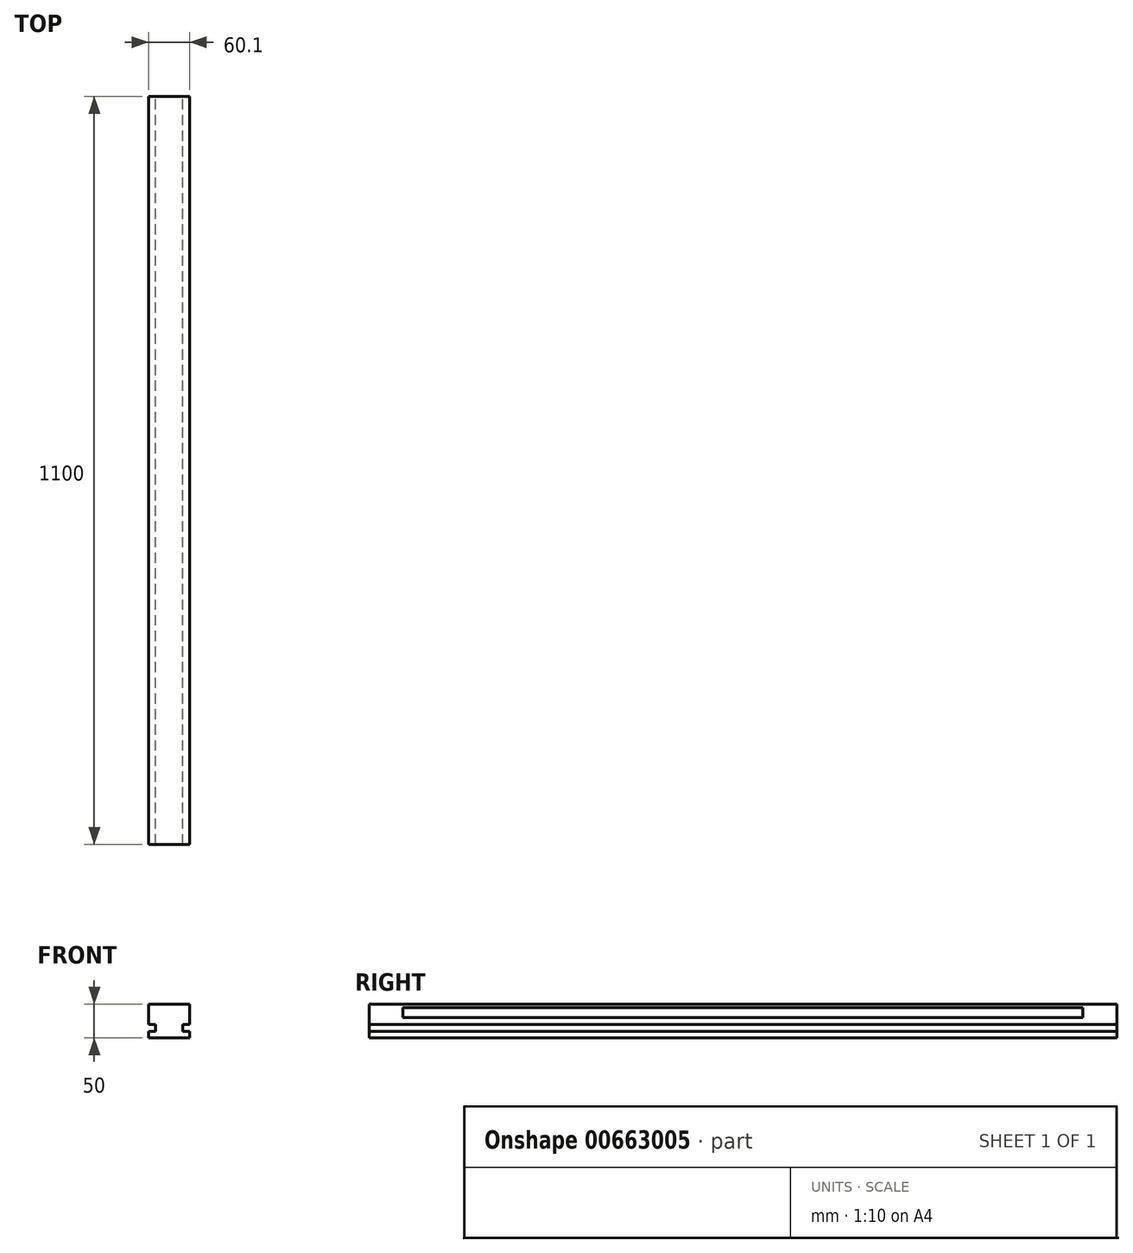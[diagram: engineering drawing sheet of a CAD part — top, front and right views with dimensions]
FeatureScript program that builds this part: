
annotation { "Feature Type Name" : "Feature", "Feature Type Description" : "" }
export const myFeature = defineFeature(function(context is Context, id is Id, definition is map)
    precondition{}
    {
        {
            var Q0;
            Q0=qCreatedBy(makeId("Front.planeOp"),FACE);
            var sketch = newSketch(context, id + "F0", { "sketchPlane" : qUnion([Q0])});
            skLineSegment(sketch, "E0", {"start": v(0, 0) * mm, "end": v(30, 0) * mm});
            skLineSegment(sketch, "E1", {"start": v(30, 0) * mm, "end": v(30, -30) * mm});
            skLineSegment(sketch, "E2", {"start": v(30, -30) * mm, "end": v(20, -30) * mm});
            skLineSegment(sketch, "E3", {"start": v(20, -30) * mm, "end": v(20, -40) * mm});
            skLineSegment(sketch, "E4", {"start": v(20, -40) * mm, "end": v(30, -40) * mm});
            skLineSegment(sketch, "E5", {"start": v(30, -40) * mm, "end": v(30, -50) * mm});
            skLineSegment(sketch, "E6", {"start": v(30, -50) * mm, "end": v(-30, -50) * mm});
            skLineSegment(sketch, "E7", {"start": v(-30, -50) * mm, "end": v(-30, -40) * mm});
            skLineSegment(sketch, "E8", {"start": v(-30, -40) * mm, "end": v(-20, -40) * mm});
            skLineSegment(sketch, "E9", {"start": v(-20, -40) * mm, "end": v(-20, -30) * mm});
            skLineSegment(sketch, "E10", {"start": v(-20, -30) * mm, "end": v(-30, -30) * mm});
            skLineSegment(sketch, "E11", {"start": v(-30, -30) * mm, "end": v(-30, 0) * mm});
            skLineSegment(sketch, "E12", {"start": v(-30, 0) * mm, "end": v(0, 0) * mm});
            skSolve(sketch);
        }
        {
            var Q0;
            Q0=makeQuery(id+"F0.imprint","IMPRINT",FACE,{"disambiguationData":[TD([[makeQuery(id+"F0.imprint","IMPRINT",EDGE,{"derivedFrom":sQuery(id+"F0.wireOp",EDGE,"E0")}),-1.0]])]});
            extrude(context, id + "F1", {"entities" : qUnion([Q0]), "depth" : 1100 * mm, "offsetDistance" : 25 * mm});
        }
        {
            var Q0;
            Q0=makeQuery(id+"F1.opExtrude","SWEPT_FACE",FACE,{"disambiguationData":[OSD([sQuery(id+"F0.wireOp",EDGE,"E1")])]});
            var sketch = newSketch(context, id + "F2", { "sketchPlane" : qUnion([Q0])});
            skLineSegment(sketch, "E13.bottom", {"start": v(-1050, -5) * mm, "end": v(-50, -5) * mm});
            skLineSegment(sketch, "E13.top", {"start": v(-1050, -20) * mm, "end": v(-50, -20) * mm});
            skLineSegment(sketch, "E13.left", {"start": v(-1050, -5) * mm, "end": v(-1050, -20) * mm});
            skLineSegment(sketch, "E13.right", {"start": v(-50, -5) * mm, "end": v(-50, -20) * mm});
            skSolve(sketch);
        }
        {
            var Q0;
            Q0=makeQuery(id+"F2.imprint","IMPRINT",FACE,{"disambiguationData":[TD([[makeQuery(id+"F2.imprint","IMPRINT",EDGE,{"derivedFrom":sQuery(id+"F2.wireOp",EDGE,"E13.bottom")}),-1.0]])]});
            extrude(context, id + "F3", {"entities" : qUnion([Q0]), "operationType" : NewBodyOperationType.ADD, "depth" : 0.1 * mm, "offsetDistance" : 25 * mm});
        }
    });
